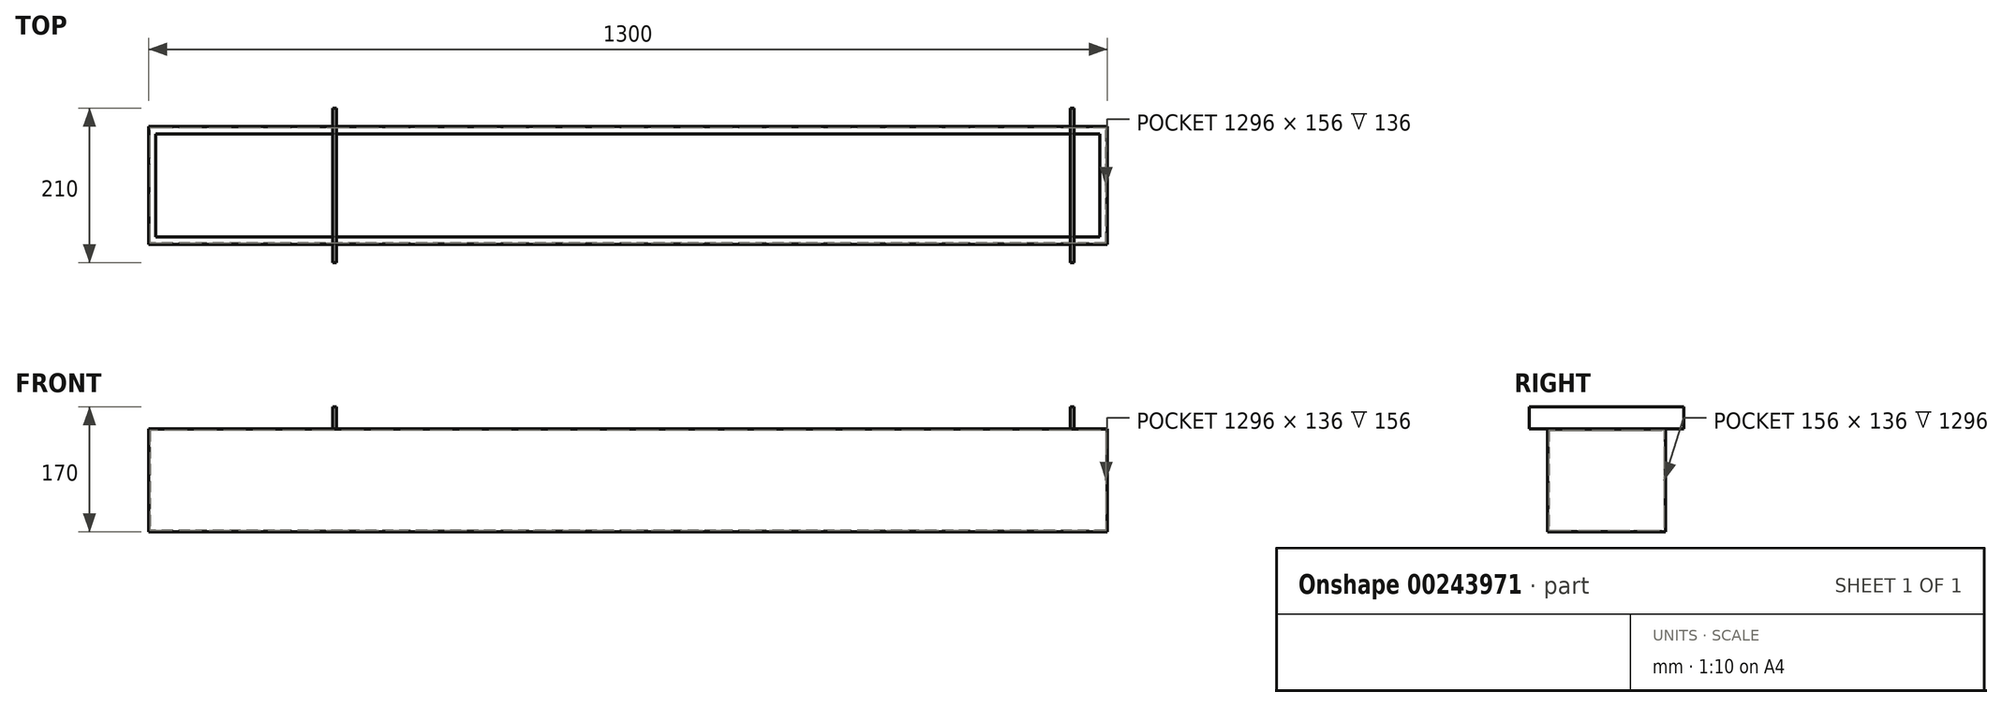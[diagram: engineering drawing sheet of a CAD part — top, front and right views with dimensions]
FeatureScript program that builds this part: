
annotation { "Feature Type Name" : "Feature", "Feature Type Description" : "" }
export const myFeature = defineFeature(function(context is Context, id is Id, definition is map)
    precondition{}
    {
        {
            var Q0;
            Q0=qCreatedBy(makeId("Right.planeOp"),FACE);
            var sketch = newSketch(context, id + "F0", { "sketchPlane" : qUnion([Q0])});
            skLineSegment(sketch, "E0.bottom", {"start": v(-76.45, 55.8) * mm, "end": v(83.55, 55.8) * mm});
            skLineSegment(sketch, "E0.top", {"start": v(-76.45, -84.2) * mm, "end": v(83.55, -84.2) * mm});
            skLineSegment(sketch, "E0.left", {"start": v(-76.45, 55.8) * mm, "end": v(-76.45, -84.2) * mm});
            skLineSegment(sketch, "E0.right", {"start": v(83.55, 55.8) * mm, "end": v(83.55, -84.2) * mm});
            skSolve(sketch);
        }
        {
            var Q0;
            Q0=makeQuery(id+"F0.imprint","IMPRINT",FACE,{"disambiguationData":[TD([[makeQuery(id+"F0.imprint","IMPRINT",EDGE,{"derivedFrom":sQuery(id+"F0.wireOp",EDGE,"E0.bottom")}),-1.0]])]});
            extrude(context, id + "F1", {"entities" : qUnion([Q0]), "depth" : 1300 * mm});
        }
        {
            var Q0;
            Q0=makeQuery(id+"F1.opExtrude","SWEPT_FACE",FACE,{"disambiguationData":[OSD([sQuery(id+"F0.wireOp",EDGE,"E0.bottom")])]});
            var sketch = newSketch(context, id + "F2", { "sketchPlane" : qUnion([Q0])});
            skLineSegment(sketch, "E1.0", {"start": v(0, -76.45) * mm, "end": v(0, 83.55) * mm});
            skLineSegment(sketch, "E2.0", {"start": v(1300, 83.55) * mm, "end": v(0, 83.55) * mm});
            skLineSegment(sketch, "E3.0", {"start": v(1300, -76.45) * mm, "end": v(1300, 83.55) * mm});
            skLineSegment(sketch, "E4.0", {"start": v(1300, -76.45) * mm, "end": v(0, -76.45) * mm});
            skLineSegment(sketch, "E5.0", {"start": v(10, -66.45) * mm, "end": v(10, 73.55) * mm});
            skLineSegment(sketch, "E5.1", {"start": v(1290, -66.45) * mm, "end": v(10, -66.45) * mm});
            skLineSegment(sketch, "E5.2", {"start": v(1290, -66.45) * mm, "end": v(1290, 73.55) * mm});
            skLineSegment(sketch, "E5.3", {"start": v(1290, 73.55) * mm, "end": v(10, 73.55) * mm});
            skSolve(sketch);
        }
        {
            var Q0;
            Q0=makeQuery(id+"F2.imprint","IMPRINT",FACE,{"disambiguationData":[TD([[makeQuery(id+"F2.imprint","IMPRINT",EDGE,{"derivedFrom":sQuery(id+"F2.wireOp",EDGE,"E5.0")}),-1.0]])]});
            extrude(context, id + "F3", {"entities" : qUnion([Q0]), "operationType" : NewBodyOperationType.REMOVE, "oppositeDirection" : true, "depth" : 2 * mm});
        }
        {
            var Q0;
            Q0=makeQuery(id+"F3.boolean.opBoolean","COPY",FACE,{"derivedFrom":makeQuery(id+"F3.opExtrude","CAP_FACE",FACE,{"disambiguationData":[OSD([sQuery(id+"F2.wireOp",EDGE,"E5.0"),sQuery(id+"F2.wireOp",EDGE,"E5.1"),sQuery(id+"F2.wireOp",EDGE,"E5.2"),sQuery(id+"F2.wireOp",EDGE,"E5.3")])],"isStart":false})});
            shell(context, id + "F4", {"entities" : qUnion([Q0]), "thickness" : 2 * mm});
        }
        {
            var Q0;
            Q0=makeQuery(id+"F1.opExtrude","SWEPT_FACE",FACE,{"disambiguationData":[OSD([sQuery(id+"F0.wireOp",EDGE,"E0.left")])]});
            var sketch = newSketch(context, id + "F5", { "sketchPlane" : qUnion([Q0])});
            skLineSegment(sketch, "E6.bottom", {"start": v(250, 55.8) * mm, "end": v(255, 55.8) * mm});
            skLineSegment(sketch, "E6.top", {"start": v(250, 85.8) * mm, "end": v(255, 85.8) * mm});
            skLineSegment(sketch, "E6.left", {"start": v(250, 55.8) * mm, "end": v(250, 85.8) * mm});
            skLineSegment(sketch, "E6.right", {"start": v(255, 55.8) * mm, "end": v(255, 85.8) * mm});
            skLineSegment(sketch, "E7.1.0.0", {"start": v(1255, 55.8) * mm, "end": v(1255, 85.8) * mm});
            skLineSegment(sketch, "E7.1.0.1", {"start": v(1250, 55.8) * mm, "end": v(1255, 55.8) * mm});
            skLineSegment(sketch, "E7.1.0.2", {"start": v(1250, 55.8) * mm, "end": v(1250, 85.8) * mm});
            skLineSegment(sketch, "E7.1.0.3", {"start": v(1250, 85.8) * mm, "end": v(1255, 85.8) * mm});
            skLineSegment(sketch, "E7.direction1", {"start": v(255, 55.8) * mm, "end": v(1255, 55.8) * mm, "construction": true});
            skSolve(sketch);
        }
        {
            var Q0;
            Q0=makeQuery(id+"F5.imprint","IMPRINT",FACE,{"disambiguationData":[TD([[makeQuery(id+"F5.imprint","IMPRINT",EDGE,{"derivedFrom":sQuery(id+"F5.wireOp",EDGE,"E6.bottom")}),-1.0]])]});
            var Q1;
            Q1=makeQuery(id+"F5.imprint","IMPRINT",FACE,{"disambiguationData":[TD([[makeQuery(id+"F5.imprint","IMPRINT",EDGE,{"derivedFrom":sQuery(id+"F5.wireOp",EDGE,"E7.1.0.0")}),1.0]])]});
            extrude(context, id + "F6", {"entities" : qUnion([Q0, Q1]), "operationType" : NewBodyOperationType.ADD, "depth" : 25 * mm, "hasSecondDirection" : true, "secondDirectionOppositeDirection" : true, "secondDirectionDepth" : 185 * mm});
        }
    });
